# Revit family: EKF_УПК_Верхний_03 отвода
name_source: partatom
category: Оборудование
units: mm (PartAtom-declared; Revit-internal decimal feet)

## family parameters
Всегда вертикально = Да
Классификация = Нет
На основе рабочей плоскости = Нет
Общий = Нет
При загрузке вырезать с полостями = Нет
Размер круглого соединителя = Использовать диаметр
Тип детали = Нормальный
Точка расчета площади = Нет

## types (2) — shared parameters
ADSK_Единица измерения = шт.
ADSK_Завод-изготовитель = Энергокомфорт
ADSK_Количество = 1
ADSK_Материал = RGB_RAL 7016 (Антрацитово-серый)
ADSK_Наименование = Узел поэтажный коллекторный
Диаметр коллектора = 57 мм
Длина коллектора = 400 мм
И01 = ♦ : 01. Узел на раме
И02 = ♦ : 02. Навесной шкаф
И03 = ♦ : 03. Встраиваемый шкаф
Изготовитель = Энергокомфорт
Количество ответвлений = 3
Кронштейн 2 = Да
Разработка семейства = https://dzen.ru
zero-valued in all types: Сортировка_Позиция

## per-type parameters (varying)
| type | Правое подключение | Шкаф_Смещение |
| УПК 3 левый | Нет | 150 мм |
| УПК 3 правый | Да | 100 мм |
